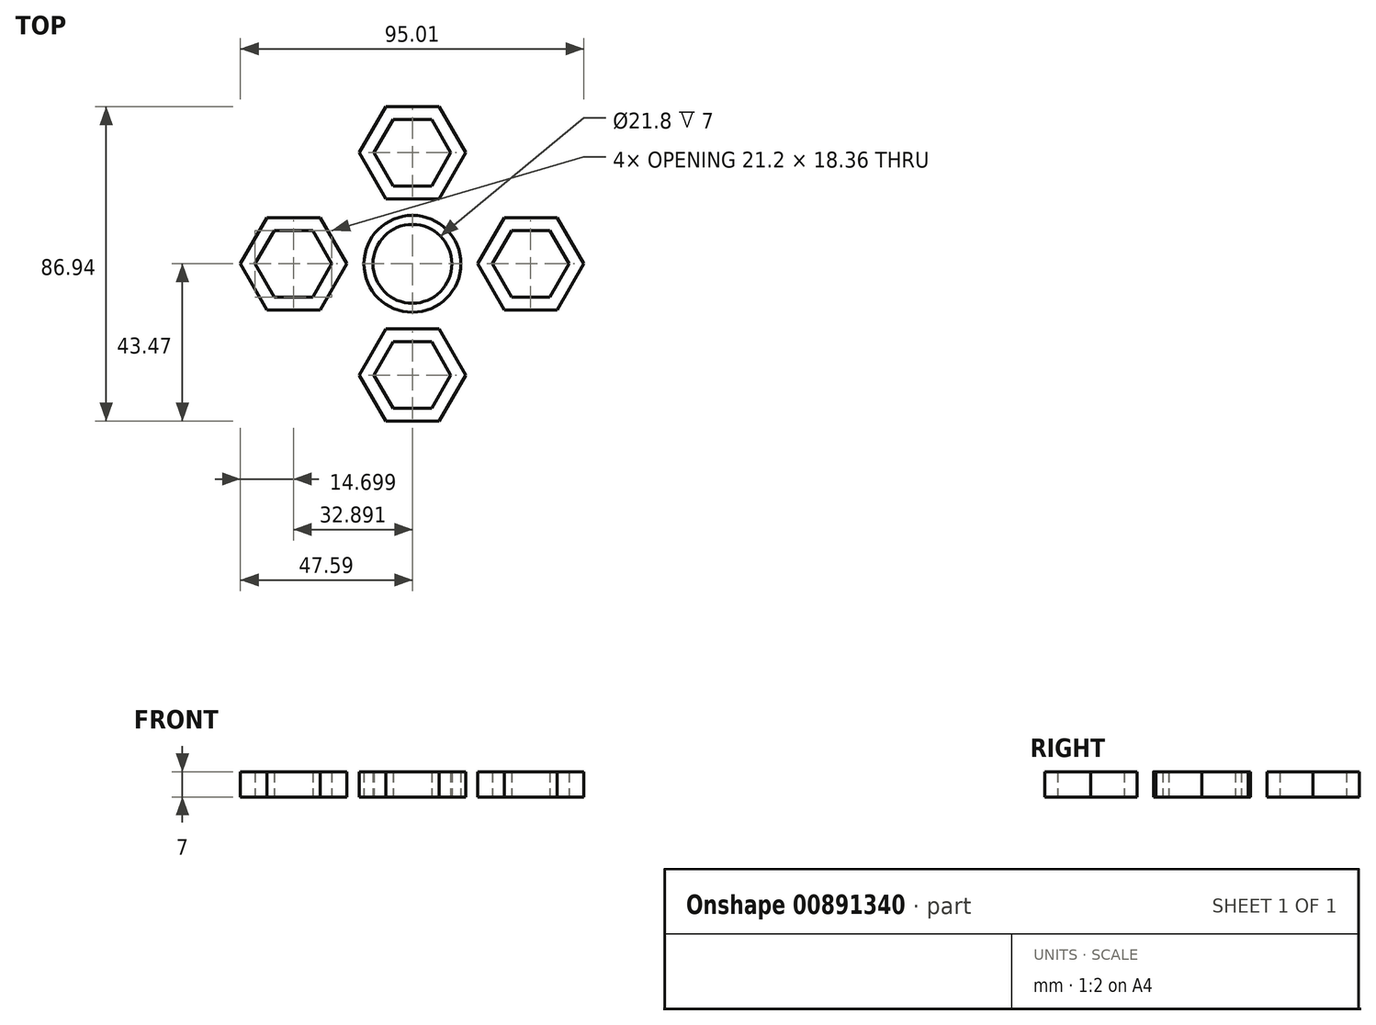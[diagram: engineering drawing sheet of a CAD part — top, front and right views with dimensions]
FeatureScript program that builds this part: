
annotation { "Feature Type Name" : "Feature", "Feature Type Description" : "" }
export const myFeature = defineFeature(function(context is Context, id is Id, definition is map)
    precondition{}
    {
        {
            var Q0;
            Q0=qCreatedBy(makeId("Top.planeOp"),FACE);
            var sketch = newSketch(context, id + "F0", { "sketchPlane" : qUnion([Q0])});
            skCircle(sketch, "E0", {"center": v(0, 0) * mm, "radius": 10.9 * mm});
            skCircle(sketch, "E1.cCircle", {"center": v(32.72, 0) * mm, "radius": 9.18 * mm, "construction": true});
            skLineSegment(sketch, "E1.0", {"start": v(27.42, 9.18) * mm, "end": v(38.02, 9.18) * mm});
            skLineSegment(sketch, "E1.1", {"start": v(38.02, 9.18) * mm, "end": v(43.32, 0) * mm});
            skLineSegment(sketch, "E1.2", {"start": v(43.32, 0) * mm, "end": v(38.02, -9.18) * mm});
            skLineSegment(sketch, "E1.3", {"start": v(38.02, -9.18) * mm, "end": v(27.42, -9.18) * mm});
            skLineSegment(sketch, "E1.4", {"start": v(27.42, -9.18) * mm, "end": v(22.12, 0) * mm});
            skLineSegment(sketch, "E1.5", {"start": v(22.12, 0) * mm, "end": v(27.42, 9.18) * mm});
            skPoint(sketch, "E1.0.midPoint", {"position": v(32.72, 9.18) * mm});
            skCircle(sketch, "E2.cCircle", {"center": v(-32.9, 0) * mm, "radius": 9.18 * mm, "construction": true});
            skLineSegment(sketch, "E2.0", {"start": v(-38.2, 9.18) * mm, "end": v(-27.6, 9.18) * mm});
            skLineSegment(sketch, "E2.1", {"start": v(-27.6, 9.18) * mm, "end": v(-22.3, 0) * mm});
            skLineSegment(sketch, "E2.2", {"start": v(-22.3, 0) * mm, "end": v(-27.6, -9.18) * mm});
            skLineSegment(sketch, "E2.3", {"start": v(-27.6, -9.18) * mm, "end": v(-38.2, -9.18) * mm});
            skLineSegment(sketch, "E2.4", {"start": v(-38.2, -9.18) * mm, "end": v(-43.5, 0) * mm});
            skLineSegment(sketch, "E2.5", {"start": v(-43.5, 0) * mm, "end": v(-38.2, 9.18) * mm});
            skPoint(sketch, "E2.0.midPoint", {"position": v(-32.9, 9.18) * mm});
            skCircle(sketch, "E3.cCircle", {"center": v(0, -30.74) * mm, "radius": 9.18 * mm, "construction": true});
            skLineSegment(sketch, "E3.0", {"start": v(-5.3, -21.56) * mm, "end": v(5.3, -21.56) * mm});
            skLineSegment(sketch, "E3.1", {"start": v(5.3, -21.56) * mm, "end": v(10.6, -30.74) * mm});
            skLineSegment(sketch, "E3.2", {"start": v(10.6, -30.74) * mm, "end": v(5.3, -39.92) * mm});
            skLineSegment(sketch, "E3.3", {"start": v(5.3, -39.92) * mm, "end": v(-5.3, -39.92) * mm});
            skLineSegment(sketch, "E3.4", {"start": v(-5.3, -39.92) * mm, "end": v(-10.6, -30.74) * mm});
            skLineSegment(sketch, "E3.5", {"start": v(-10.6, -30.74) * mm, "end": v(-5.3, -21.56) * mm});
            skPoint(sketch, "E3.0.midPoint", {"position": v(0, -21.56) * mm});
            skCircle(sketch, "E4.cCircle", {"center": v(0, 30.74) * mm, "radius": 9.18 * mm, "construction": true});
            skLineSegment(sketch, "E4.0", {"start": v(-5.3, 39.92) * mm, "end": v(5.3, 39.92) * mm});
            skLineSegment(sketch, "E4.1", {"start": v(5.3, 39.92) * mm, "end": v(10.6, 30.74) * mm});
            skLineSegment(sketch, "E4.2", {"start": v(10.6, 30.74) * mm, "end": v(5.3, 21.56) * mm});
            skLineSegment(sketch, "E4.3", {"start": v(5.3, 21.56) * mm, "end": v(-5.3, 21.56) * mm});
            skLineSegment(sketch, "E4.4", {"start": v(-5.3, 21.56) * mm, "end": v(-10.6, 30.74) * mm});
            skLineSegment(sketch, "E4.5", {"start": v(-10.6, 30.74) * mm, "end": v(-5.3, 39.92) * mm});
            skPoint(sketch, "E4.0.midPoint", {"position": v(0, 39.92) * mm});
            skCircle(sketch, "E5.cCircle", {"center": v(-32.9, 0) * mm, "radius": 12.73 * mm, "construction": true});
            skLineSegment(sketch, "E5.0", {"start": v(-40.24, 12.73) * mm, "end": v(-25.54, 12.73) * mm});
            skLineSegment(sketch, "E5.1", {"start": v(-25.54, 12.73) * mm, "end": v(-18.2, 0) * mm});
            skLineSegment(sketch, "E5.2", {"start": v(-18.2, 0) * mm, "end": v(-25.54, -12.73) * mm});
            skLineSegment(sketch, "E5.3", {"start": v(-25.54, -12.73) * mm, "end": v(-40.24, -12.73) * mm});
            skLineSegment(sketch, "E5.4", {"start": v(-40.24, -12.73) * mm, "end": v(-47.6, 0) * mm});
            skLineSegment(sketch, "E5.5", {"start": v(-47.6, 0) * mm, "end": v(-40.24, 12.73) * mm});
            skPoint(sketch, "E5.0.midPoint", {"position": v(-32.9, 12.73) * mm});
            skCircle(sketch, "E6.cCircle", {"center": v(0, 30.74) * mm, "radius": 12.73 * mm, "construction": true});
            skLineSegment(sketch, "E6.0", {"start": v(-7.35, 43.47) * mm, "end": v(7.35, 43.47) * mm});
            skLineSegment(sketch, "E6.1", {"start": v(7.35, 43.47) * mm, "end": v(14.7, 30.74) * mm});
            skLineSegment(sketch, "E6.2", {"start": v(14.7, 30.74) * mm, "end": v(7.35, 18.01) * mm});
            skLineSegment(sketch, "E6.3", {"start": v(7.35, 18.01) * mm, "end": v(-7.35, 18.01) * mm});
            skLineSegment(sketch, "E6.4", {"start": v(-7.35, 18.01) * mm, "end": v(-14.7, 30.74) * mm});
            skLineSegment(sketch, "E6.5", {"start": v(-14.7, 30.74) * mm, "end": v(-7.35, 43.47) * mm});
            skPoint(sketch, "E6.0.midPoint", {"position": v(0, 43.47) * mm});
            skCircle(sketch, "E7.cCircle", {"center": v(32.72, 0) * mm, "radius": 12.73 * mm, "construction": true});
            skLineSegment(sketch, "E7.0", {"start": v(25.37, 12.73) * mm, "end": v(40.07, 12.73) * mm});
            skLineSegment(sketch, "E7.1", {"start": v(40.07, 12.73) * mm, "end": v(47.42, 0) * mm});
            skLineSegment(sketch, "E7.2", {"start": v(47.42, 0) * mm, "end": v(40.07, -12.73) * mm});
            skLineSegment(sketch, "E7.3", {"start": v(40.07, -12.73) * mm, "end": v(25.37, -12.73) * mm});
            skLineSegment(sketch, "E7.4", {"start": v(25.37, -12.73) * mm, "end": v(18.02, 0) * mm});
            skLineSegment(sketch, "E7.5", {"start": v(18.02, 0) * mm, "end": v(25.37, 12.73) * mm});
            skPoint(sketch, "E7.0.midPoint", {"position": v(32.72, 12.73) * mm});
            skCircle(sketch, "E8.cCircle", {"center": v(0, -30.74) * mm, "radius": 12.73 * mm, "construction": true});
            skLineSegment(sketch, "E8.0", {"start": v(-7.35, -18.01) * mm, "end": v(7.35, -18.01) * mm});
            skLineSegment(sketch, "E8.1", {"start": v(7.35, -18.01) * mm, "end": v(14.7, -30.74) * mm});
            skLineSegment(sketch, "E8.2", {"start": v(14.7, -30.74) * mm, "end": v(7.35, -43.47) * mm});
            skLineSegment(sketch, "E8.3", {"start": v(7.35, -43.47) * mm, "end": v(-7.35, -43.47) * mm});
            skLineSegment(sketch, "E8.4", {"start": v(-7.35, -43.47) * mm, "end": v(-14.7, -30.74) * mm});
            skLineSegment(sketch, "E8.5", {"start": v(-14.7, -30.74) * mm, "end": v(-7.35, -18.01) * mm});
            skPoint(sketch, "E8.0.midPoint", {"position": v(0, -18.01) * mm});
            skCircle(sketch, "E9", {"center": v(0, 0) * mm, "radius": 13.4 * mm});
            skLineSegment(sketch, "E10", {"start": v(0, -10.9) * mm, "end": v(0, -17.9) * mm});
            skLineSegment(sketch, "E11", {"start": v(10.9, 0) * mm, "end": v(17.9, 0) * mm});
            skLineSegment(sketch, "E12", {"start": v(0, 10.9) * mm, "end": v(0, 17.9) * mm});
            skLineSegment(sketch, "E13", {"start": v(-10.9, 0) * mm, "end": v(-17.9, 0) * mm});
            skSolve(sketch);
        }
        {
            var Q0;
            Q0=makeQuery(id+"F0.imprint","IMPRINT",FACE,{"disambiguationData":[TD([[makeQuery(id+"F0.imprint","IMPRINT",EDGE,{"derivedFrom":sQuery(id+"F0.wireOp",EDGE,"E2.0")}),1.0]])]});
            var Q1;
            {var subQ3=sQuery(id+"F0.wireOp",EDGE,"JlrCRoD2-8TIj-y38s-t6qC-ggU2A914CWM4");Q1=makeQuery(id+"F0.imprint","IMPRINT",FACE,{"disambiguationData":[TD([[makeQuery(id+"F0.imprint","IMPRINT",EDGE,{"derivedFrom":subQ3}),1.0]])]});}
            var Q2;
            {var subQ3=sQuery(id+"F0.wireOp",EDGE,"mmWBLaqN-dRE9-k8lS-uMR3-XbLHIxNOZDcg");Q2=makeQuery(id+"F0.imprint","IMPRINT",FACE,{"disambiguationData":[TD([[makeQuery(id+"F0.imprint","IMPRINT",EDGE,{"derivedFrom":subQ3}),-1.0]])]});}
            var Q3;
            {var subQ4=sQuery(id+"F0.wireOp",EDGE,"E12");var subQ5=sQuery(id+"F0.wireOp",EDGE,"E0");var subQ6=makeQuery(id+"F0.imprint","INTERSECT",VERTEX,{"derivedFrom":[subQ5,subQ4]});Q3=makeQuery(id+"F0.imprint","IMPRINT",FACE,{"disambiguationData":[TD([[makeQuery(id+"F0.imprint","IMPRINT",EDGE,{"disambiguationData":[TD([[subQ6,-1.0]])],"derivedFrom":subQ5}),-1.0]])]});}
            var Q4;
            {var subQ5=sQuery(id+"F0.wireOp",EDGE,"E11");var subQ7=sQuery(id+"F0.wireOp",EDGE,"E0");var subQ8=makeQuery(id+"F0.imprint","INTERSECT",VERTEX,{"derivedFrom":[subQ7,subQ5]});Q4=makeQuery(id+"F0.imprint","IMPRINT",FACE,{"disambiguationData":[TD([[makeQuery(id+"F0.imprint","IMPRINT",EDGE,{"disambiguationData":[TD([[subQ8,-1.0]])],"derivedFrom":subQ7}),-1.0]])]});}
            var Q5;
            {var subQ3=sQuery(id+"F0.wireOp",EDGE,"E10");var subQ7=sQuery(id+"F0.wireOp",EDGE,"E0");var subQ8=makeQuery(id+"F0.imprint","INTERSECT",VERTEX,{"derivedFrom":[subQ7,subQ3]});Q5=makeQuery(id+"F0.imprint","IMPRINT",FACE,{"disambiguationData":[TD([[makeQuery(id+"F0.imprint","IMPRINT",EDGE,{"disambiguationData":[TD([[subQ8,-1.0]])],"derivedFrom":subQ7}),-1.0]])]});}
            var Q6;
            {var subQ2=sQuery(id+"F0.wireOp",EDGE,"E10");var subQ7=sQuery(id+"F0.wireOp",EDGE,"E0");var subQ9=makeQuery(id+"F0.imprint","INTERSECT",VERTEX,{"derivedFrom":[subQ7,subQ2]});Q6=makeQuery(id+"F0.imprint","IMPRINT",FACE,{"disambiguationData":[TD([[makeQuery(id+"F0.imprint","IMPRINT",EDGE,{"disambiguationData":[TD([[subQ9,1.0]])],"derivedFrom":subQ7}),-1.0]])]});}
            var Q7;
            {var subQ0=sQuery(id+"F0.wireOp",EDGE,"8pKirDAM-W3mh-FW36-Xi1O-lb0F8bI7rKhc");Q7=makeQuery(id+"F0.imprint","IMPRINT",FACE,{"disambiguationData":[TD([[makeQuery(id+"F0.imprint","IMPRINT",EDGE,{"derivedFrom":subQ0}),-1.0]])]});}
            var Q8;
            {var subQ0=sQuery(id+"F0.wireOp",EDGE,"Xex6JAWp-dtQa-RTqy-PI0t-Ykg4ocZOFsmm");Q8=makeQuery(id+"F0.imprint","IMPRINT",FACE,{"disambiguationData":[TD([[makeQuery(id+"F0.imprint","IMPRINT",EDGE,{"derivedFrom":subQ0}),1.0]])]});}
            var Q9;
            {var subQ3=sQuery(id+"F0.wireOp",EDGE,"F7ElJsGd-Oaos-JHGh-i4n2-MgRu9Iny8MqQ");Q9=makeQuery(id+"F0.imprint","IMPRINT",FACE,{"disambiguationData":[TD([[makeQuery(id+"F0.imprint","IMPRINT",EDGE,{"derivedFrom":subQ3}),-1.0]])]});}
            var Q10;
            {var subQ3=sQuery(id+"F0.wireOp",EDGE,"UhS1Ea3W-l36b-Yojj-xaif-7HpRSaUcUjOA");Q10=makeQuery(id+"F0.imprint","IMPRINT",FACE,{"disambiguationData":[TD([[makeQuery(id+"F0.imprint","IMPRINT",EDGE,{"derivedFrom":subQ3}),1.0]])]});}
            var Q11;
            Q11=makeQuery(id+"F0.imprint","IMPRINT",FACE,{"disambiguationData":[TD([[makeQuery(id+"F0.imprint","IMPRINT",EDGE,{"derivedFrom":sQuery(id+"F0.wireOp",EDGE,"E3.0")}),1.0]])]});
            var Q12;
            Q12=makeQuery(id+"F0.imprint","IMPRINT",FACE,{"disambiguationData":[TD([[makeQuery(id+"F0.imprint","IMPRINT",EDGE,{"derivedFrom":sQuery(id+"F0.wireOp",EDGE,"E1.0")}),1.0]])]});
            var Q13;
            Q13=makeQuery(id+"F0.imprint","IMPRINT",FACE,{"disambiguationData":[TD([[makeQuery(id+"F0.imprint","IMPRINT",EDGE,{"derivedFrom":sQuery(id+"F0.wireOp",EDGE,"E4.0")}),1.0]])]});
            var Q14;
            Q14=makeQuery(id+"F0.imprint","IMPRINT",FACE,{"disambiguationData":[TD([[makeQuery(id+"F0.imprint","IMPRINT",EDGE,{"derivedFrom":sQuery(id+"F0.wireOp",EDGE,"E6.3")}),1.0]])]});
            extrude(context, id + "F1", {"entities" : qUnion([Q0, Q1, Q2, Q3, Q4, Q5, Q6, Q7, Q8, Q9, Q10, Q11, Q12, Q13, Q14]), "depth" : 7 * mm, "offsetDistance" : 25 * mm});
        }
    });
